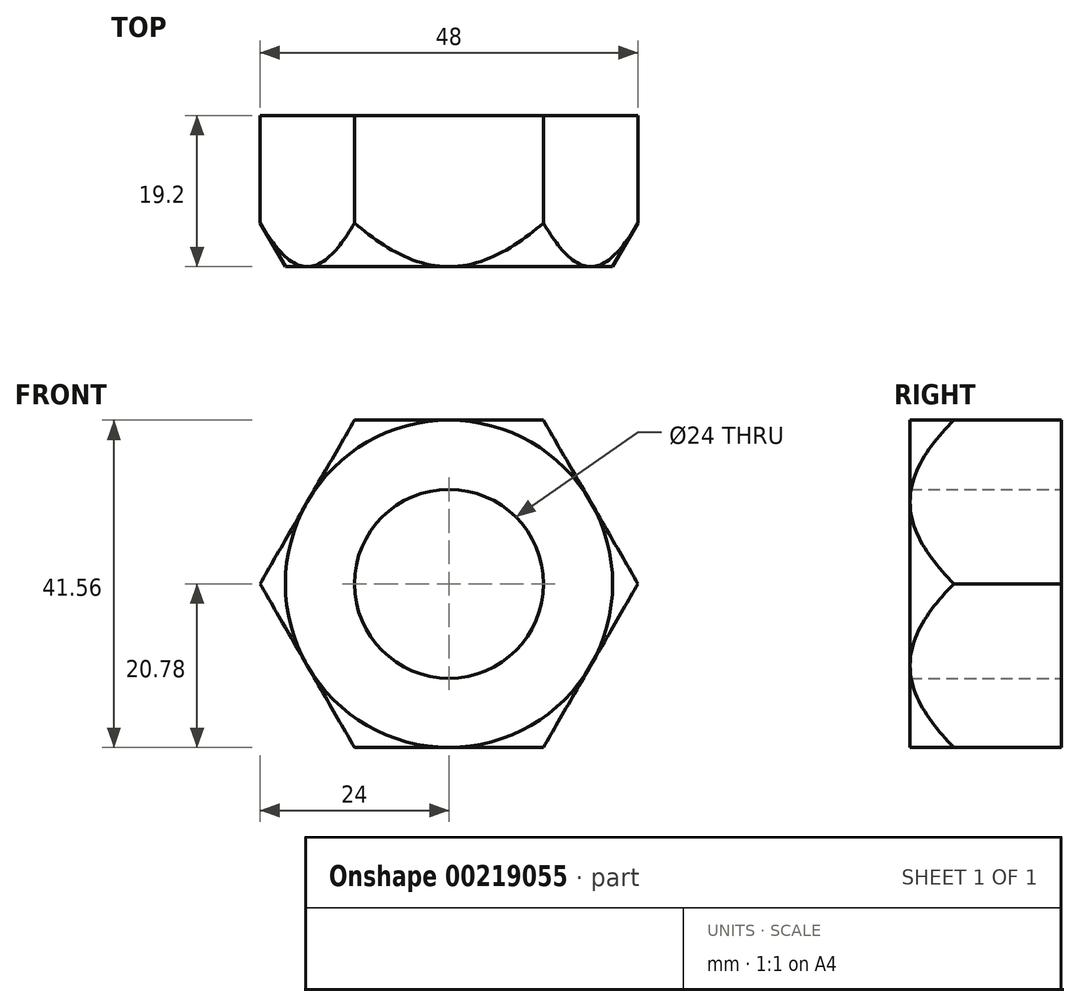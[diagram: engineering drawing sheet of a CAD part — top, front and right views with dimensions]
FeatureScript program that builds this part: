
annotation { "Feature Type Name" : "Feature", "Feature Type Description" : "" }
export const myFeature = defineFeature(function(context is Context, id is Id, definition is map)
    precondition{}
    {
        {
            var Q0;
            Q0=qCreatedBy(makeId("Front.planeOp"),FACE);
            var sketch = newSketch(context, id + "F0", { "sketchPlane" : qUnion([Q0])});
            skCircle(sketch, "E0.cCircle", {"center": v(0, 0) * mm, "radius": 24 * mm, "construction": true});
            skLineSegment(sketch, "E0.0", {"start": v(-12, 20.78) * mm, "end": v(12, 20.78) * mm});
            skLineSegment(sketch, "E0.1", {"start": v(12, 20.78) * mm, "end": v(24, 0) * mm});
            skLineSegment(sketch, "E0.2", {"start": v(24, 0) * mm, "end": v(12, -20.78) * mm});
            skLineSegment(sketch, "E0.3", {"start": v(12, -20.78) * mm, "end": v(-12, -20.78) * mm});
            skLineSegment(sketch, "E0.4", {"start": v(-12, -20.78) * mm, "end": v(-24, 0) * mm});
            skLineSegment(sketch, "E0.5", {"start": v(-24, 0) * mm, "end": v(-12, 20.78) * mm});
            skCircle(sketch, "E1", {"center": v(0, 0) * mm, "radius": 12 * mm});
            skSolve(sketch);
        }
        {
            var Q0;
            Q0 = qSketchRegion(id + "F0", true);
            extrude(context, id + "F1", {"entities" : qUnion([Q0]), "depth" : (0.8 * 24) * mm});
        }
        {
            var Q0;
            Q0=makeQuery(id+"F1.opExtrude","CAP_FACE",FACE,{"disambiguationData":[OSD([sQuery(id+"F0.wireOp",EDGE,"E0.0"),sQuery(id+"F0.wireOp",EDGE,"E0.1"),sQuery(id+"F0.wireOp",EDGE,"E0.2"),sQuery(id+"F0.wireOp",EDGE,"E0.3"),sQuery(id+"F0.wireOp",EDGE,"E0.4"),sQuery(id+"F0.wireOp",EDGE,"E0.5"),sQuery(id+"F0.wireOp",EDGE,"E1")])],"isStart":false});
            var sketch = newSketch(context, id + "F2", { "sketchPlane" : qUnion([Q0])});
            skCircle(sketch, "E2", {"center": v(0, 0) * mm, "radius": 20.78 * mm});
            skSolve(sketch);
        }
        {
            var Q0;
            Q0=qCreatedBy(makeId("Top.planeOp"),FACE);
            var sketch = newSketch(context, id + "F3", { "sketchPlane" : qUnion([Q0])});
            skLineSegment(sketch, "E3.0", {"start": v(20.78, -19.2) * mm, "end": v(-20.78, -19.2) * mm, "construction": true});
            skLineSegment(sketch, "E4", {"start": v(20.78, -19.2) * mm, "end": v(24, -13.63) * mm});
            skLineSegment(sketch, "E5", {"start": v(24, -13.63) * mm, "end": v(24, -19.2) * mm});
            skLineSegment(sketch, "E6", {"start": v(24, -19.2) * mm, "end": v(20.78, -19.2) * mm});
            skLineSegment(sketch, "E7", {"start": v(0, -29.9) * mm, "end": v(0, 2.54) * mm});
            skSolve(sketch);
        }
        {
            var Q0;
            Q0 = qSketchRegion(id + "F3", true);
            var Q1;
            Q1=sQuery(id+"F3.wireOp",EDGE,"E7");
            revolve(context, id + "F4", {"operationType" : NewBodyOperationType.REMOVE, "entities" : qUnion([Q0]), "axis" : qUnion([Q1]), "revolveType" : RevolveType.FULL, "oppositeDirection" : true});
        }
    });
